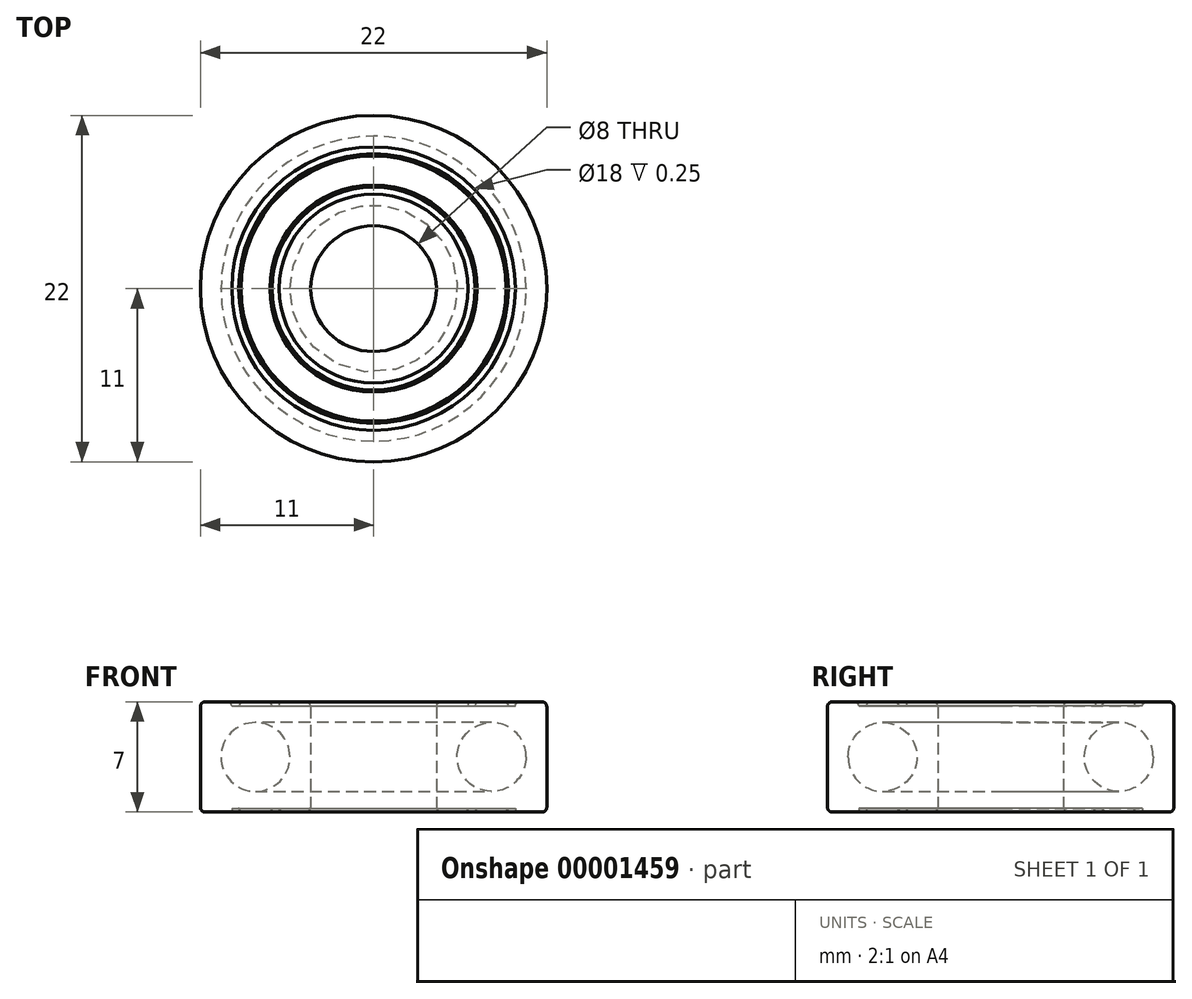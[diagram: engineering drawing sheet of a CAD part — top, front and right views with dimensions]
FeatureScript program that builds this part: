
annotation { "Feature Type Name" : "Feature", "Feature Type Description" : "" }
export const myFeature = defineFeature(function(context is Context, id is Id, definition is map)
    precondition{}
    {
        {
            var Q0;
            Q0=qCreatedBy(makeId("Front.planeOp"),FACE);
            var sketch = newSketch(context, id + "F0", { "sketchPlane" : qUnion([Q0])});
            skLineSegment(sketch, "E0", {"start": v(0, 0) * mm, "end": v(4, 0) * mm, "construction": true});
            skLineSegment(sketch, "E1", {"start": v(4, 0) * mm, "end": v(4, -3.5) * mm});
            skLineSegment(sketch, "E2", {"start": v(4, -3.5) * mm, "end": v(6, -3.5) * mm});
            skLineSegment(sketch, "E3", {"start": v(6, -3.5) * mm, "end": v(6, -3.25) * mm});
            skLineSegment(sketch, "E4", {"start": v(6, -3.25) * mm, "end": v(6.44, -3.25) * mm});
            skLineSegment(sketch, "E5", {"start": v(6.44, -3.25) * mm, "end": v(6.58, -3.5) * mm});
            skLineSegment(sketch, "E6", {"start": v(6.58, -3.5) * mm, "end": v(8.42, -3.5) * mm});
            skLineSegment(sketch, "E7", {"start": v(8.42, -3.5) * mm, "end": v(8.56, -3.25) * mm});
            skLineSegment(sketch, "E8", {"start": v(8.56, -3.25) * mm, "end": v(9, -3.25) * mm});
            skLineSegment(sketch, "E9", {"start": v(9, -3.25) * mm, "end": v(9, -3.5) * mm});
            skLineSegment(sketch, "E10", {"start": v(9, -3.5) * mm, "end": v(11, -3.5) * mm});
            skLineSegment(sketch, "E11", {"start": v(11, -3.5) * mm, "end": v(11, 0) * mm});
            skLineSegment(sketch, "E12.0.MirrorCS", {"start": v(4, 3.5) * mm, "end": v(6, 3.5) * mm});
            skLineSegment(sketch, "E12.1.MirrorCS", {"start": v(11, 3.5) * mm, "end": v(11, 0) * mm});
            skLineSegment(sketch, "E12.2.MirrorCS", {"start": v(4, 0) * mm, "end": v(4, 3.5) * mm});
            skLineSegment(sketch, "E12.3.MirrorCS", {"start": v(6, 3.25) * mm, "end": v(6.44, 3.25) * mm});
            skLineSegment(sketch, "E12.4.MirrorCS", {"start": v(9, 3.25) * mm, "end": v(9, 3.5) * mm});
            skLineSegment(sketch, "E12.5.MirrorCS", {"start": v(6.44, 3.25) * mm, "end": v(6.58, 3.5) * mm});
            skLineSegment(sketch, "E12.6.MirrorCS", {"start": v(6.58, 3.5) * mm, "end": v(8.42, 3.5) * mm});
            skLineSegment(sketch, "E12.7.MirrorCS", {"start": v(8.42, 3.5) * mm, "end": v(8.56, 3.25) * mm});
            skLineSegment(sketch, "E12.8.MirrorCS", {"start": v(9, 3.5) * mm, "end": v(11, 3.5) * mm});
            skLineSegment(sketch, "E12.9.MirrorCS", {"start": v(6, 3.5) * mm, "end": v(6, 3.25) * mm});
            skLineSegment(sketch, "E12.10.MirrorCS", {"start": v(8.56, 3.25) * mm, "end": v(9, 3.25) * mm});
            skLineSegment(sketch, "E13", {"start": v(0, 0) * mm, "end": v(0, 5.44) * mm, "construction": true});
            skLineSegment(sketch, "E14", {"start": v(0, 0) * mm, "end": v(-4, 0) * mm, "construction": true});
            skLineSegment(sketch, "E15", {"start": v(4, 0) * mm, "end": v(11, 0) * mm, "construction": true});
            skLineSegment(sketch, "E16", {"start": v(-4, 0) * mm, "end": v(-11, 0) * mm, "construction": true});
            skCircle(sketch, "E17", {"center": v(7.5, 0) * mm, "radius": 2.19 * mm});
            skSolve(sketch);
        }
        {
            var Q0;
            Q0=makeQuery(id+"F0.imprint","IMPRINT",FACE,{"disambiguationData":[TD([[makeQuery(id+"F0.imprint","IMPRINT",EDGE,{"derivedFrom":sQuery(id+"F0.wireOp",EDGE,"E2")}),1.0]])]});
            var Q1;
            Q1=sQuery(id+"F0.wireOp",EDGE,"E13");
            revolve(context, id + "F1", {"entities" : qUnion([Q0]), "axis" : qUnion([Q1]), "revolveType" : RevolveType.FULL});
        }
        {
            var Q0;
            Q0=makeQuery(id+"F1.opRevolve","SWEPT_EDGE",EDGE,{"disambiguationData":[OSD([sQuery(id+"F0.wireOp",EDGE,"E11"),sQuery(id+"F0.wireOp",EDGE,"E12.8.MirrorCS")])]});
            var Q1;
            Q1=makeQuery(id+"F1.opRevolve","SWEPT_EDGE",EDGE,{"disambiguationData":[OSD([sQuery(id+"F0.wireOp",EDGE,"E12.0.MirrorCS"),sQuery(id+"F0.wireOp",EDGE,"E12.2.MirrorCS")])]});
            var Q2;
            Q2=makeQuery(id+"F1.opRevolve","SWEPT_EDGE",EDGE,{"disambiguationData":[OSD([sQuery(id+"F0.wireOp",EDGE,"E10"),sQuery(id+"F0.wireOp",EDGE,"E11")])]});
            var Q3;
            Q3=makeQuery(id+"F1.opRevolve","SWEPT_EDGE",EDGE,{"disambiguationData":[OSD([sQuery(id+"F0.wireOp",EDGE,"E2"),sQuery(id+"F0.wireOp",EDGE,"E12.2.MirrorCS")])]});
            fillet(context, id + "F2", {"entities" : qUnion([Q0, Q1, Q2, Q3]), "radius" : .3 * mm, "tangentPropagation" : true, "allowEdgeOverflow" : false});
        }
    });
